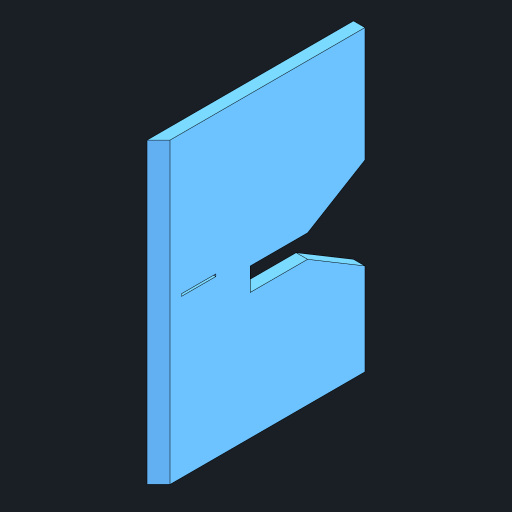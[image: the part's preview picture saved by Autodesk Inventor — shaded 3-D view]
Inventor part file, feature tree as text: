
AUTODESK INVENTOR PART (.ipt)
format: ipt  version: 2023 (Build 270158000, 158)  size: 131,072 bytes
history: native  units: mm
features: extrude x2, sketch x2, other x1, chamfer x1
ambient origin geometry x8: Origin, YZ Plane, XZ Plane, XY Plane, X Axis, Y Axis, Z Axis, Center Point
bodies: Body1 (feature_tree)
feature tree (6):
  other  "ソリッド1"
  extrude  "押し出し1"  Depth=130.0mm
  extrude  "押し出し3"  Depth=40.0mm
  chamfer  "面取り1"  Distance=5.0mm
  sketch  "スケッチ1"
  sketch  "スケッチ3"
